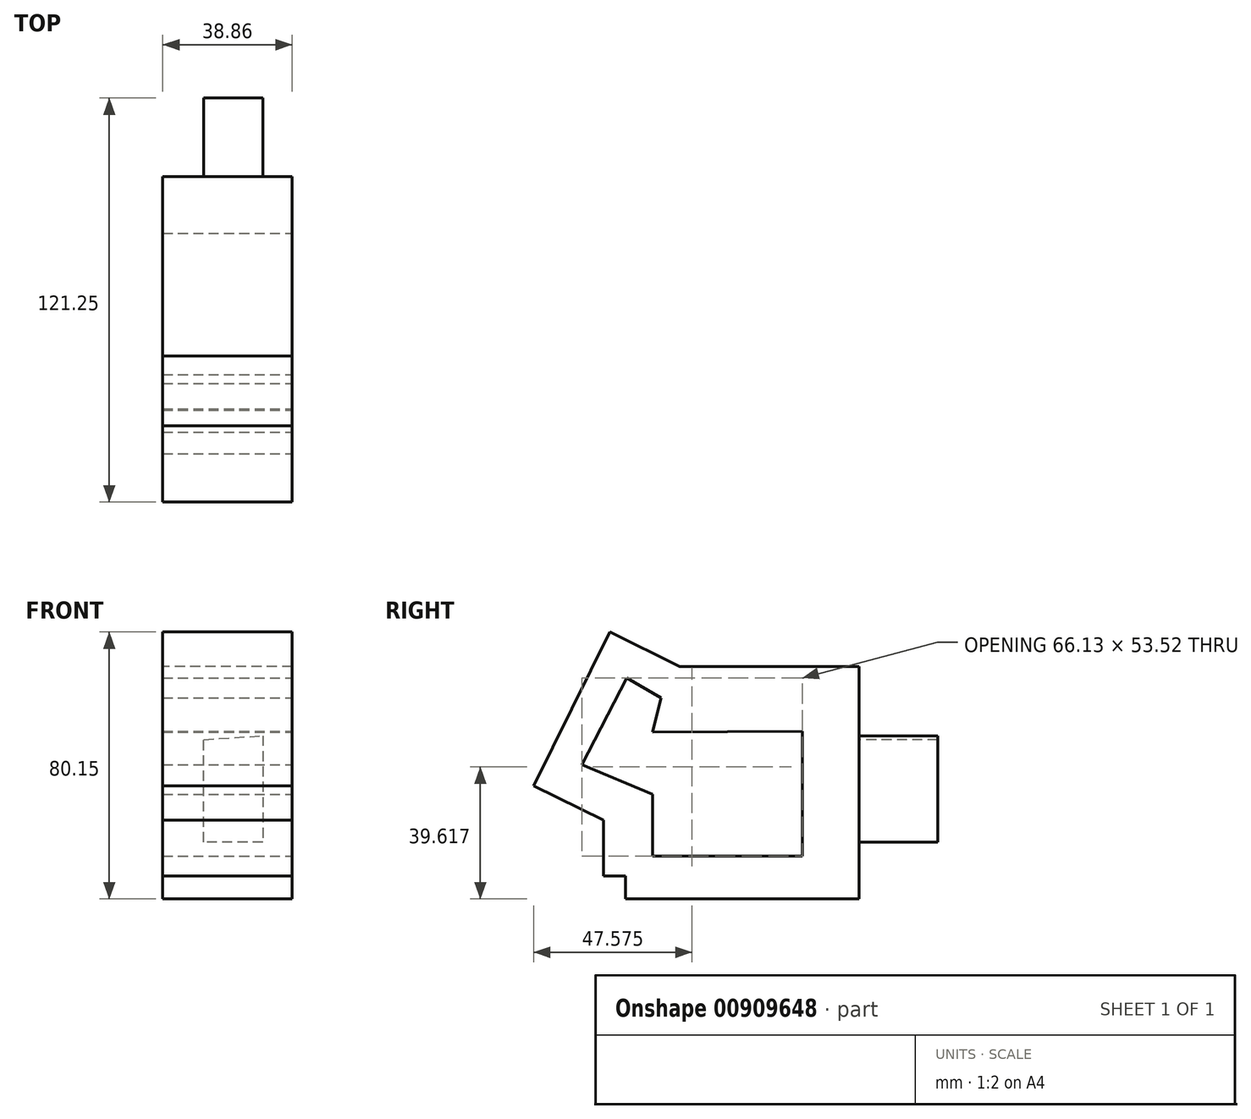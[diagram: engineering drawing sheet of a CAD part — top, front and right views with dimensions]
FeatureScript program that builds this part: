
annotation { "Feature Type Name" : "Feature", "Feature Type Description" : "" }
export const myFeature = defineFeature(function(context is Context, id is Id, definition is map)
    precondition{}
    {
        {
            var Q0;
            Q0=qCreatedBy(makeId("Right.planeOp"),FACE);
            var sketch = newSketch(context, id + "F0", { "sketchPlane" : qUnion([Q0])});
            skLineSegment(sketch, "E0", {"start": v(-22.46, 23.88) * mm, "end": v(31.34, 23.88) * mm});
            skLineSegment(sketch, "E1", {"start": v(31.34, 23.88) * mm, "end": v(31.34, -22.27) * mm});
            skLineSegment(sketch, "E2", {"start": v(31.34, -22.27) * mm, "end": v(-45.35, -22.27) * mm});
            skLineSegment(sketch, "E3", {"start": v(-45.35, -22.27) * mm, "end": v(-22.46, 23.88) * mm});
            skSolve(sketch);
        }
        {
            var Q0;
            Q0=makeQuery(id+"F0.imprint","IMPRINT",FACE,{"disambiguationData":[TD([[makeQuery(id+"F0.imprint","IMPRINT",EDGE,{"derivedFrom":sQuery(id+"F0.wireOp",EDGE,"E0")}),-1.0]])]});
            extrude(context, id + "F1", {"entities" : qUnion([Q0]), "depth" : 38.86 * mm, "offsetDistance" : 25.4 * mm});
        }
        {
            var Q0;
            Q0=makeQuery(id+"F1.opExtrude","SWEPT_FACE",FACE,{"disambiguationData":[OSD([sQuery(id+"F0.wireOp",EDGE,"E0")])]});
            var Q1;
            Q1=makeQuery(id+"F1.opExtrude","SWEPT_FACE",FACE,{"disambiguationData":[OSD([sQuery(id+"F0.wireOp",EDGE,"E3")])]});
            extrude(context, id + "F2", {"entities" : qUnion([Q0, Q1]), "operationType" : NewBodyOperationType.ADD, "depth" : 23.62 * mm, "offsetDistance" : 25.4 * mm});
        }
        {
            var Q0;
            Q0=makeQuery(id+"F2.opExtrude","CAP_FACE",FACE,{"disambiguationData":[OSD([sQuery(id+"F0.wireOp",EDGE,"E3")]),OD(1.0)],"isStart":false});
            extrude(context, id + "F3", {"entities" : qUnion([Q0]), "operationType" : NewBodyOperationType.ADD, "depth" : 23.37 * mm, "offsetDistance" : 25.4 * mm});
        }
        {
            var Q0;
            {var subQ0=sQuery(id+"F0.wireOp",EDGE,"E3");var subQ1=makeQuery(id+"F1.opExtrude","CAP_EDGE",EDGE,{"disambiguationData":[OSD([subQ0])],"isStart":false});var subQ2=sQuery(id+"F0.wireOp",EDGE,"E0");Q0=makeQuery(id+"F3.boolean.opBoolean","MERGE",FACE,{"derivedFrom":[makeQuery(id+"F2.boolean.opBoolean","MERGE",FACE,{"derivedFrom":[makeQuery(id+"F1.opExtrude","CAP_FACE",FACE,{"disambiguationData":[OSD([subQ2,sQuery(id+"F0.wireOp",EDGE,"E1"),sQuery(id+"F0.wireOp",EDGE,"E2"),subQ0])],"isStart":false}),makeQuery(id+"F2.opExtrude","SWEPT_FACE",FACE,{"disambiguationData":[OSD([subQ2]),TDD([makeQuery(id+"F1.opExtrude","CAP_EDGE",EDGE,{"disambiguationData":[OSD([subQ2])],"isStart":false})])]}),makeQuery(id+"F2.opExtrude","SWEPT_FACE",FACE,{"disambiguationData":[OSD([subQ0]),TDD([subQ1])]})]}),makeQuery(id+"F3.opExtrude","SWEPT_FACE",FACE,{"disambiguationData":[OSD([subQ0]),TDD([makeQuery(id+"F2.opExtrude","CAP_EDGE",EDGE,{"disambiguationData":[OSD([subQ0]),TDD([subQ1]),OD(1.0)],"isStart":false})])]})]});}
            var sketch = newSketch(context, id + "F4", { "sketchPlane" : qUnion([Q0])});
            skLineSegment(sketch, "E4", {"start": v(-30.65, 27.78) * mm, "end": v(-30.65, -9.41) * mm});
            skLineSegment(sketch, "E5", {"start": v(-30.65, -9.41) * mm, "end": v(14.35, -9.41) * mm});
            skLineSegment(sketch, "E6", {"start": v(14.35, -9.41) * mm, "end": v(14.35, 28) * mm});
            skLineSegment(sketch, "E7", {"start": v(14.35, 28) * mm, "end": v(-30.65, 27.78) * mm});
            skSolve(sketch);
        }
        {
            var Q0;
            Q0=makeQuery(id+"F4.imprint","IMPRINT",FACE,{"disambiguationData":[TD([[makeQuery(id+"F4.imprint","IMPRINT",EDGE,{"derivedFrom":sQuery(id+"F4.wireOp",EDGE,"E4")}),1.0]])]});
            extrude(context, id + "F5", {"entities" : qUnion([Q0]), "operationType" : NewBodyOperationType.REMOVE, "oppositeDirection" : true, "depth" : 79.25 * mm, "offsetDistance" : 25.4 * mm});
        }
        {
            var Q0;
            {var subQ0=sQuery(id+"F0.wireOp",EDGE,"E3");var subQ1=makeQuery(id+"F1.opExtrude","CAP_EDGE",EDGE,{"disambiguationData":[OSD([subQ0])],"isStart":false});var subQ2=sQuery(id+"F0.wireOp",EDGE,"E0");Q0=makeQuery(id+"F3.boolean.opBoolean","MERGE",FACE,{"derivedFrom":[makeQuery(id+"F2.boolean.opBoolean","MERGE",FACE,{"derivedFrom":[makeQuery(id+"F1.opExtrude","CAP_FACE",FACE,{"disambiguationData":[OSD([subQ2,sQuery(id+"F0.wireOp",EDGE,"E1"),sQuery(id+"F0.wireOp",EDGE,"E2"),subQ0])],"isStart":false}),makeQuery(id+"F2.opExtrude","SWEPT_FACE",FACE,{"disambiguationData":[OSD([subQ2]),TDD([makeQuery(id+"F1.opExtrude","CAP_EDGE",EDGE,{"disambiguationData":[OSD([subQ2])],"isStart":false})])]}),makeQuery(id+"F2.opExtrude","SWEPT_FACE",FACE,{"disambiguationData":[OSD([subQ0]),TDD([subQ1])]})]}),makeQuery(id+"F3.opExtrude","SWEPT_FACE",FACE,{"disambiguationData":[OSD([subQ0]),TDD([makeQuery(id+"F2.opExtrude","CAP_EDGE",EDGE,{"disambiguationData":[OSD([subQ0]),TDD([subQ1]),OD(1.0)],"isStart":false})])]})]});}
            var sketch = newSketch(context, id + "F6", { "sketchPlane" : qUnion([Q0])});
            skLineSegment(sketch, "E8", {"start": v(-38.28, 44.1) * mm, "end": v(-51.78, 18) * mm});
            skLineSegment(sketch, "E9", {"start": v(-51.78, 18) * mm, "end": v(-30.65, 9.18) * mm});
            skLineSegment(sketch, "E10", {"start": v(-30.65, 9.18) * mm, "end": v(-30.65, 27.78) * mm});
            skLineSegment(sketch, "E11", {"start": v(-30.65, 27.78) * mm, "end": v(-28, 38.1) * mm});
            skLineSegment(sketch, "E12", {"start": v(-28, 38.1) * mm, "end": v(-38.28, 44.1) * mm});
            skSolve(sketch);
        }
        {
            var Q0;
            Q0 = qSketchRegion(id + "F6", true);
            extrude(context, id + "F7", {"entities" : qUnion([Q0]), "operationType" : NewBodyOperationType.REMOVE, "oppositeDirection" : true, "depth" : 75.7 * mm, "offsetDistance" : 25.4 * mm});
        }
        {
            var Q0;
            {var subQ0=sQuery(id+"F0.wireOp",EDGE,"E3");var subQ1=makeQuery(id+"F1.opExtrude","CAP_EDGE",EDGE,{"disambiguationData":[OSD([subQ0])],"isStart":false});var subQ2=sQuery(id+"F0.wireOp",EDGE,"E0");Q0=makeQuery(id+"F3.boolean.opBoolean","MERGE",FACE,{"derivedFrom":[makeQuery(id+"F2.boolean.opBoolean","MERGE",FACE,{"derivedFrom":[makeQuery(id+"F1.opExtrude","CAP_FACE",FACE,{"disambiguationData":[OSD([subQ2,sQuery(id+"F0.wireOp",EDGE,"E1"),sQuery(id+"F0.wireOp",EDGE,"E2"),subQ0])],"isStart":false}),makeQuery(id+"F2.opExtrude","SWEPT_FACE",FACE,{"disambiguationData":[OSD([subQ2]),TDD([makeQuery(id+"F1.opExtrude","CAP_EDGE",EDGE,{"disambiguationData":[OSD([subQ2])],"isStart":false})])]}),makeQuery(id+"F2.opExtrude","SWEPT_FACE",FACE,{"disambiguationData":[OSD([subQ0]),TDD([subQ1])]})]}),makeQuery(id+"F3.opExtrude","SWEPT_FACE",FACE,{"disambiguationData":[OSD([subQ0]),TDD([makeQuery(id+"F2.opExtrude","CAP_EDGE",EDGE,{"disambiguationData":[OSD([subQ0]),TDD([subQ1]),OD(1.0)],"isStart":false})])]})]});}
            var sketch = newSketch(context, id + "F8", { "sketchPlane" : qUnion([Q0])});
            skLineSegment(sketch, "E13", {"start": v(-45.35, -15.38) * mm, "end": v(-38.68, -15.38) * mm});
            skLineSegment(sketch, "E14", {"start": v(-38.68, -15.38) * mm, "end": v(-38.68, -22.27) * mm});
            skLineSegment(sketch, "E15", {"start": v(-38.68, -22.27) * mm, "end": v(-45.35, -22.27) * mm});
            skLineSegment(sketch, "E16", {"start": v(-45.35, -22.27) * mm, "end": v(-45.35, -15.38) * mm});
            skSolve(sketch);
        }
        {
            var Q0;
            Q0 = qSketchRegion(id + "F8", true);
            extrude(context, id + "F9", {"entities" : qUnion([Q0]), "operationType" : NewBodyOperationType.REMOVE, "oppositeDirection" : true, "depth" : 99.31 * mm, "offsetDistance" : 25.4 * mm});
        }
        {
            var Q0;
            {var subQ0=sQuery(id+"F0.wireOp",EDGE,"E1");Q0=makeQuery(id+"F2.boolean.opBoolean","MERGE",FACE,{"derivedFrom":[makeQuery(id+"F1.opExtrude","SWEPT_FACE",FACE,{"disambiguationData":[OSD([subQ0])]}),makeQuery(id+"F2.opExtrude","SWEPT_FACE",FACE,{"disambiguationData":[OSD([sQuery(id+"F0.wireOp",EDGE,"E0"),subQ0])]})]});}
            var sketch = newSketch(context, id + "F10", { "sketchPlane" : qUnion([Q0])});
            skLineSegment(sketch, "E17", {"start": v(-30.06, 26.7) * mm, "end": v(-30.06, -5.19) * mm});
            skLineSegment(sketch, "E18", {"start": v(-30.06, -5.19) * mm, "end": v(-12.34, -5.19) * mm});
            skLineSegment(sketch, "E19", {"start": v(-12.34, -5.19) * mm, "end": v(-12.34, 25.59) * mm});
            skLineSegment(sketch, "E20", {"start": v(-12.34, 25.59) * mm, "end": v(-30.06, 26.7) * mm});
            skSolve(sketch);
        }
        {
            var Q0;
            Q0 = qSketchRegion(id + "F10", true);
            extrude(context, id + "F11", {"entities" : qUnion([Q0]), "operationType" : NewBodyOperationType.ADD, "depth" : 23.62 * mm, "offsetDistance" : 25.4 * mm});
        }
    });
